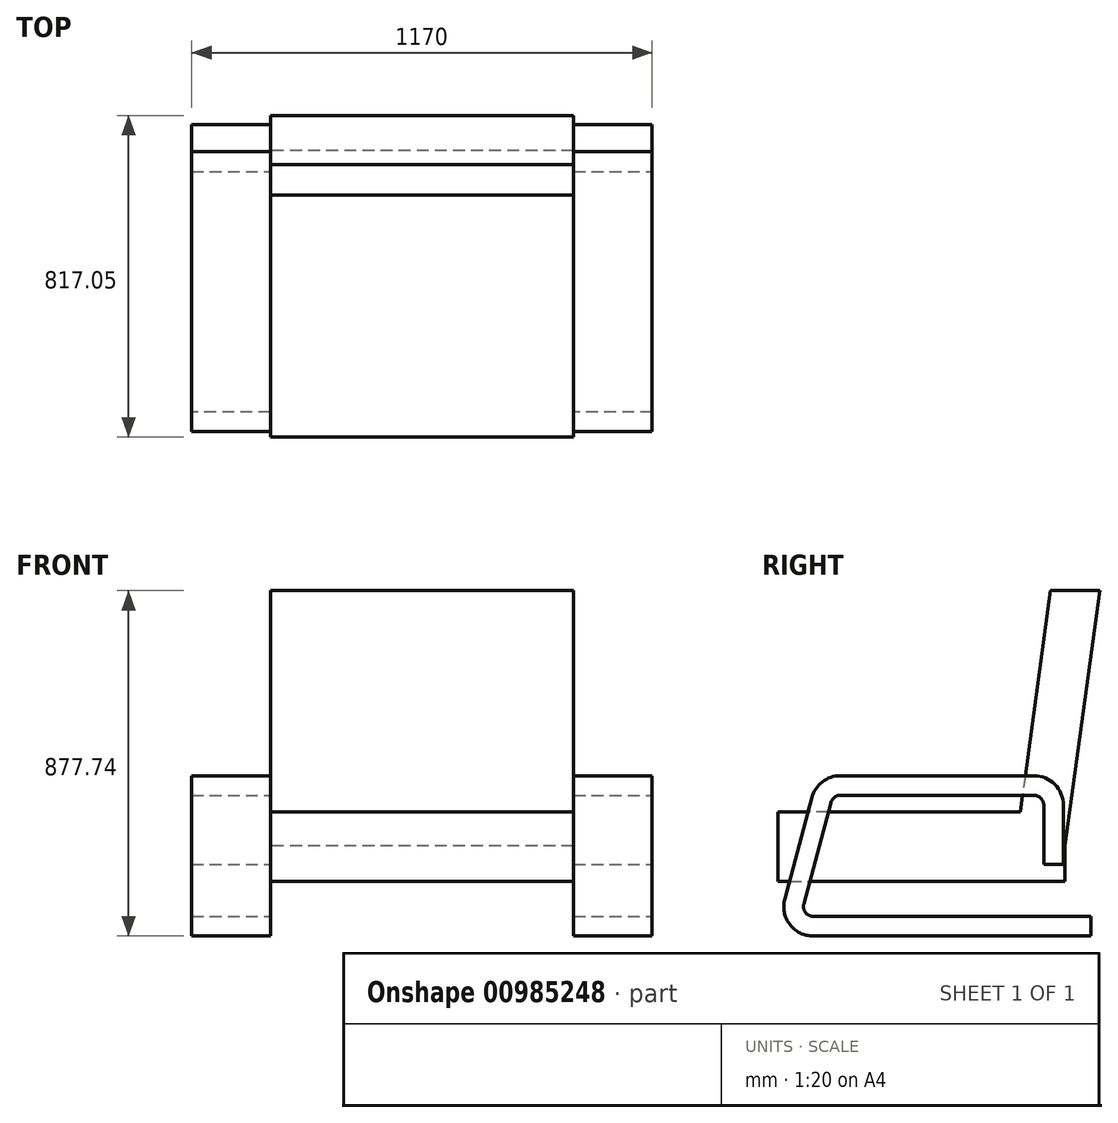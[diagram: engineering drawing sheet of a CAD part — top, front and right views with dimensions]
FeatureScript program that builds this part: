
annotation { "Feature Type Name" : "Feature", "Feature Type Description" : "" }
export const myFeature = defineFeature(function(context is Context, id is Id, definition is map)
    precondition{}
    {
        {
            var Q0;
            Q0=qCreatedBy(makeId("Right.planeOp"),FACE);
            var sketch = newSketch(context, id + "F0", { "sketchPlane" : qUnion([Q0])});
            skLineSegment(sketch, "E0", {"start": v(65.9, 70.28) * mm, "end": v(-638.93, 70.28) * mm});
            skLineSegment(sketch, "E1", {"start": v(-687.23, 133.22) * mm, "end": v(-618.26, 390.62) * mm});
            skLineSegment(sketch, "E2", {"start": v(-569.96, 427.67) * mm, "end": v(-78.33, 427.67) * mm});
            skLineSegment(sketch, "E3", {"start": v(-28.33, 377.67) * mm, "end": v(-28.33, 227.67) * mm});
            skPoint(sketch, "E4.visualSharp", {"position": v(-608.33, 427.67) * mm});
            skArc(sketch, "E4.filletArc", {"start": v(-569.96, 427.67) * mm, "mid": v(-600.4, 417.34) * mm, "end": v(-618.26, 390.62) * mm});
            skPoint(sketch, "E5.visualSharp", {"position": v(-704.1, 70.28) * mm});
            skArc(sketch, "E5.filletArc", {"start": v(-687.23, 133.22) * mm, "mid": v(-678.6, 89.84) * mm, "end": v(-638.93, 70.28) * mm});
            skPoint(sketch, "E6.visualSharp", {"position": v(-28.33, 427.67) * mm});
            skArc(sketch, "E6.filletArc", {"start": v(-28.33, 377.67) * mm, "mid": v(-42.98, 413.03) * mm, "end": v(-78.33, 427.67) * mm});
            skSolve(sketch);
        }
        {
            var Q0;
            Q0=qCreatedBy(makeId("Front.planeOp"),FACE);
            var sketch = newSketch(context, id + "F1", { "sketchPlane" : qUnion([Q0])});
            skLineSegment(sketch, "E7.bottom", {"start": v(-585, 45.28) * mm, "end": v(585, 45.28) * mm});
            skLineSegment(sketch, "E7.top", {"start": v(-585, 95.28) * mm, "end": v(585, 95.28) * mm});
            skLineSegment(sketch, "E7.left", {"start": v(-585, 45.28) * mm, "end": v(-585, 95.28) * mm});
            skLineSegment(sketch, "E7.right", {"start": v(585, 45.28) * mm, "end": v(585, 95.28) * mm});
            skPoint(sketch, "E7.middle", {"position": v(0, 70.28) * mm});
            skSolve(sketch);
        }
        {
            var Q0;
            Q0=makeQuery(id+"F1.imprint","IMPRINT",FACE,{"disambiguationData":[TD([[makeQuery(id+"F1.imprint","IMPRINT",EDGE,{"derivedFrom":sQuery(id+"F1.wireOp",EDGE,"E7.bottom")}),1.0]])]});
            var Q1;
            Q1=sQuery(id+"F0.wireOp",EDGE,"E0");
            var Q2;
            Q2=sQuery(id+"F0.wireOp",EDGE,"E5.filletArc");
            var Q3;
            Q3=sQuery(id+"F0.wireOp",EDGE,"E1");
            var Q4;
            Q4=sQuery(id+"F0.wireOp",EDGE,"E4.filletArc");
            var Q5;
            Q5=sQuery(id+"F0.wireOp",EDGE,"E2");
            var Q6;
            Q6=sQuery(id+"F0.wireOp",EDGE,"E6.filletArc");
            var Q7;
            Q7=sQuery(id+"F0.wireOp",EDGE,"E3");
            sweep(context, id + "F2", {"profiles" : qUnion([Q0]), "path" : qUnion([Q1, Q2, Q3, Q4, Q5, Q6, Q7])});
        }
        {
            var Q0;
            Q0=qCreatedBy(makeId("Top.planeOp"),FACE);
            var sketch = newSketch(context, id + "F3", { "sketchPlane" : qUnion([Q0])});
            skLineSegment(sketch, "E8.bottom", {"start": v(385, -761.24) * mm, "end": v(-385, -761.24) * mm});
            skLineSegment(sketch, "E8.top", {"start": v(385, 138.76) * mm, "end": v(-385, 138.76) * mm});
            skLineSegment(sketch, "E8.left", {"start": v(385, -761.24) * mm, "end": v(385, 138.76) * mm});
            skLineSegment(sketch, "E8.right", {"start": v(-385, -761.24) * mm, "end": v(-385, 138.76) * mm});
            skPoint(sketch, "E8.middle", {"position": v(0, -311.24) * mm});
            skSolve(sketch);
        }
        {
            var Q0;
            Q0 = qSketchRegion(id + "F3", true);
            extrude(context, id + "F4", {"entities" : qUnion([Q0]), "operationType" : NewBodyOperationType.REMOVE, "depth" : 600 * mm, "offsetDistance" : 25 * mm});
        }
        {
            var Q0;
            Q0=qCreatedBy(makeId("Right.planeOp"),FACE);
            var sketch = newSketch(context, id + "F5", { "sketchPlane" : qUnion([Q0])});
            skLineSegment(sketch, "E9", {"start": v(-728.07, 274.1) * mm, "end": v(0, 274.1) * mm});
            skLineSegment(sketch, "E10", {"start": v(-113.07, 361.08) * mm, "end": v(-728.07, 361.08) * mm});
            skLineSegment(sketch, "E11", {"start": v(-728.07, 361.08) * mm, "end": v(-728.07, 274.1) * mm});
            skLineSegment(sketch, "E12", {"start": v(0, 274.1) * mm, "end": v(88.98, 923.02) * mm});
            skLineSegment(sketch, "E13", {"start": v(88.98, 923.02) * mm, "end": v(-36.02, 923.02) * mm});
            skLineSegment(sketch, "E14", {"start": v(-36.02, 923.02) * mm, "end": v(-113.07, 361.08) * mm});
            skSolve(sketch);
        }
        {
            var Q0;
            Q0 = qSketchRegion(id + "F5", true);
            var Q1;
            {var subQ0=sQuery(id+"F1.wireOp",EDGE,"E7.top");Q1=makeQuery(id+"F4.boolean.opBoolean","INTERSECT",VERTEX,{"derivedFrom":[makeQuery(id+"F2.opSweep","SWEPT_FACE",FACE,{"disambiguationData":[OSD([sQuery(id+"F0.wireOp",EDGE,"E1"),subQ0])]}),makeQuery(id+"F2.opSweep","SWEPT_FACE",FACE,{"disambiguationData":[OSD([sQuery(id+"F0.wireOp",EDGE,"E4.filletArc"),subQ0])]}),makeQuery(id+"F4.opExtrude","SWEPT_FACE",FACE,{"disambiguationData":[OSD([sQuery(id+"F3.wireOp",EDGE,"E8.left")])]})]});}
            extrude(context, id + "F6", {"entities" : qUnion([Q0]), "endBound" : BoundingType.UP_TO_VERTEX, "depth" : 25 * mm, "endBoundEntityVertex" : qUnion([Q1]), "offsetDistance" : 25 * mm});
        }
        {
            var Q0;
            Q0=makeQuery(id+"F6.opExtrude","CAP_FACE",FACE,{"disambiguationData":[OSD([sQuery(id+"F5.wireOp",EDGE,"E9"),sQuery(id+"F5.wireOp",EDGE,"E10"),sQuery(id+"F5.wireOp",EDGE,"E11"),sQuery(id+"F5.wireOp",EDGE,"E12"),sQuery(id+"F5.wireOp",EDGE,"E13"),sQuery(id+"F5.wireOp",EDGE,"E14")])],"isStart":true});
            var Q1;
            {var subQ0=sQuery(id+"F1.wireOp",EDGE,"E7.top");Q1=makeQuery(id+"F4.boolean.opBoolean","INTERSECT",VERTEX,{"derivedFrom":[makeQuery(id+"F2.opSweep","SWEPT_FACE",FACE,{"disambiguationData":[OSD([sQuery(id+"F0.wireOp",EDGE,"E1"),subQ0])]}),makeQuery(id+"F2.opSweep","SWEPT_FACE",FACE,{"disambiguationData":[OSD([sQuery(id+"F0.wireOp",EDGE,"E4.filletArc"),subQ0])]}),makeQuery(id+"F4.opExtrude","SWEPT_FACE",FACE,{"disambiguationData":[OSD([sQuery(id+"F3.wireOp",EDGE,"E8.right")])]})]});}
            extrude(context, id + "F7", {"entities" : qUnion([Q0]), "operationType" : NewBodyOperationType.ADD, "endBound" : BoundingType.UP_TO_VERTEX, "depth" : 25 * mm, "endBoundEntityVertex" : qUnion([Q1]), "offsetDistance" : 25 * mm});
        }
        {
            var Q0;
            {var subQ0=sQuery(id+"F5.wireOp",EDGE,"E9");Q0=makeQuery(id+"F7.boolean.opBoolean","MERGE",FACE,{"derivedFrom":[makeQuery(id+"F6.opExtrude","SWEPT_FACE",FACE,{"disambiguationData":[OSD([subQ0])]}),makeQuery(id+"F7.opExtrude","SWEPT_FACE",FACE,{"disambiguationData":[OSD([subQ0])]})]});}
            extrude(context, id + "F8", {"entities" : qUnion([Q0]), "operationType" : NewBodyOperationType.ADD, "depth" : 90 * mm, "offsetDistance" : 25 * mm});
        }
    });
